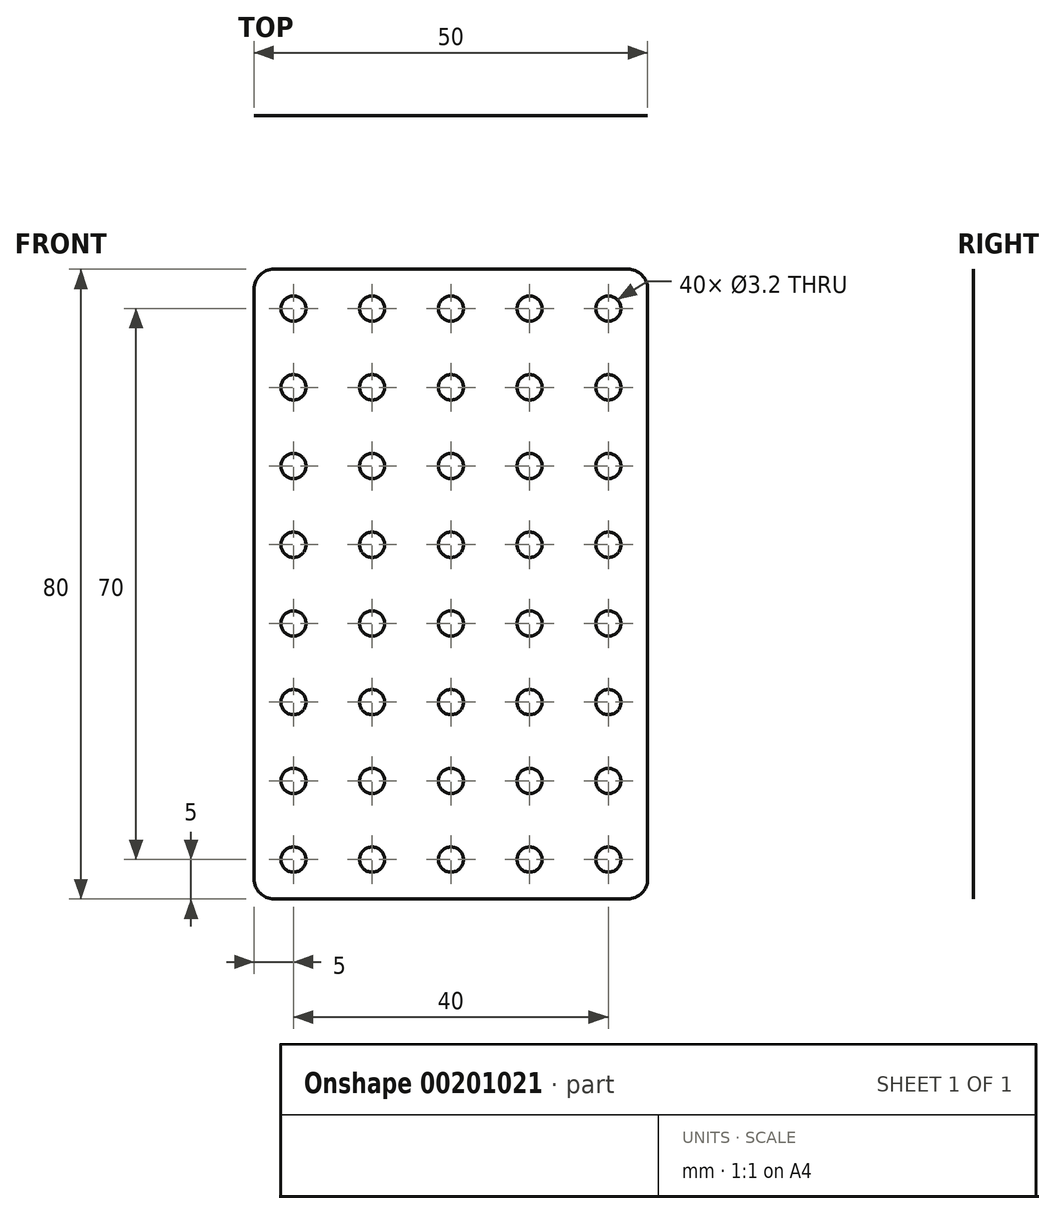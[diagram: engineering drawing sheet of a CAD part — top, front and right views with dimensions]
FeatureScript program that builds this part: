
annotation { "Feature Type Name" : "Feature", "Feature Type Description" : "" }
export const myFeature = defineFeature(function(context is Context, id is Id, definition is map)
    precondition{}
    {
        {
            var Q0;
            Q0=qCreatedBy(makeId("Front.planeOp"),FACE);
            var sketch = newSketch(context, id + "F0", { "sketchPlane" : qUnion([Q0])});
            skLineSegment(sketch, "E0.bottom", {"start": v(2.54, 0) * mm, "end": v(47.46, 0) * mm});
            skLineSegment(sketch, "E0.top", {"start": v(2.54, -80) * mm, "end": v(47.46, -80) * mm});
            skLineSegment(sketch, "E0.left", {"start": v(0, -2.54) * mm, "end": v(0, -77.46) * mm});
            skLineSegment(sketch, "E0.right", {"start": v(50, -2.54) * mm, "end": v(50, -77.46) * mm});
            skPoint(sketch, "E1.visualSharp", {"position": v(0, 0) * mm});
            skArc(sketch, "E1.filletArc", {"start": v(2.54, 0) * mm, "mid": v(0.74, -0.74) * mm, "end": v(0, -2.54) * mm});
            skPoint(sketch, "E2.visualSharp", {"position": v(50, 0) * mm});
            skArc(sketch, "E2.filletArc", {"start": v(50, -2.54) * mm, "mid": v(49.26, -0.74) * mm, "end": v(47.46, 0) * mm});
            skPoint(sketch, "E3.visualSharp", {"position": v(0, -80) * mm});
            skArc(sketch, "E3.filletArc", {"start": v(0, -77.46) * mm, "mid": v(0.74, -79.26) * mm, "end": v(2.54, -80) * mm});
            skPoint(sketch, "E4.visualSharp", {"position": v(50, -80) * mm});
            skArc(sketch, "E4.filletArc", {"start": v(47.46, -80) * mm, "mid": v(49.26, -79.26) * mm, "end": v(50, -77.46) * mm});
            skCircle(sketch, "E5", {"center": v(5, -5) * mm, "radius": 1.6 * mm});
            skCircle(sketch, "E6.0.1.0", {"center": v(5, -15) * mm, "radius": 1.6 * mm});
            skCircle(sketch, "E6.0.2.0", {"center": v(5, -25) * mm, "radius": 1.6 * mm});
            skCircle(sketch, "E6.0.3.0", {"center": v(5, -35) * mm, "radius": 1.6 * mm});
            skCircle(sketch, "E6.0.4.0", {"center": v(5, -45) * mm, "radius": 1.6 * mm});
            skCircle(sketch, "E6.0.5.0", {"center": v(5, -55) * mm, "radius": 1.6 * mm});
            skCircle(sketch, "E6.0.6.0", {"center": v(5, -65) * mm, "radius": 1.6 * mm});
            skCircle(sketch, "E6.0.7.0", {"center": v(5, -75) * mm, "radius": 1.6 * mm});
            skCircle(sketch, "E6.1.0.0", {"center": v(15, -5) * mm, "radius": 1.6 * mm});
            skCircle(sketch, "E6.1.1.0", {"center": v(15, -15) * mm, "radius": 1.6 * mm});
            skCircle(sketch, "E6.1.2.0", {"center": v(15, -25) * mm, "radius": 1.6 * mm});
            skCircle(sketch, "E6.1.3.0", {"center": v(15, -35) * mm, "radius": 1.6 * mm});
            skCircle(sketch, "E6.1.4.0", {"center": v(15, -45) * mm, "radius": 1.6 * mm});
            skCircle(sketch, "E6.1.5.0", {"center": v(15, -55) * mm, "radius": 1.6 * mm});
            skCircle(sketch, "E6.1.6.0", {"center": v(15, -65) * mm, "radius": 1.6 * mm});
            skCircle(sketch, "E6.1.7.0", {"center": v(15, -75) * mm, "radius": 1.6 * mm});
            skCircle(sketch, "E6.2.0.0", {"center": v(25, -5) * mm, "radius": 1.6 * mm});
            skCircle(sketch, "E6.2.1.0", {"center": v(25, -15) * mm, "radius": 1.6 * mm});
            skCircle(sketch, "E6.2.2.0", {"center": v(25, -25) * mm, "radius": 1.6 * mm});
            skCircle(sketch, "E6.2.3.0", {"center": v(25, -35) * mm, "radius": 1.6 * mm});
            skCircle(sketch, "E6.2.4.0", {"center": v(25, -45) * mm, "radius": 1.6 * mm});
            skCircle(sketch, "E6.2.5.0", {"center": v(25, -55) * mm, "radius": 1.6 * mm});
            skCircle(sketch, "E6.2.6.0", {"center": v(25, -65) * mm, "radius": 1.6 * mm});
            skCircle(sketch, "E6.2.7.0", {"center": v(25, -75) * mm, "radius": 1.6 * mm});
            skCircle(sketch, "E6.3.0.0", {"center": v(35, -5) * mm, "radius": 1.6 * mm});
            skCircle(sketch, "E6.3.1.0", {"center": v(35, -15) * mm, "radius": 1.6 * mm});
            skCircle(sketch, "E6.3.2.0", {"center": v(35, -25) * mm, "radius": 1.6 * mm});
            skCircle(sketch, "E6.3.3.0", {"center": v(35, -35) * mm, "radius": 1.6 * mm});
            skCircle(sketch, "E6.3.4.0", {"center": v(35, -45) * mm, "radius": 1.6 * mm});
            skCircle(sketch, "E6.3.5.0", {"center": v(35, -55) * mm, "radius": 1.6 * mm});
            skCircle(sketch, "E6.3.6.0", {"center": v(35, -65) * mm, "radius": 1.6 * mm});
            skCircle(sketch, "E6.3.7.0", {"center": v(35, -75) * mm, "radius": 1.6 * mm});
            skCircle(sketch, "E6.4.0.0", {"center": v(45, -5) * mm, "radius": 1.6 * mm});
            skCircle(sketch, "E6.4.1.0", {"center": v(45, -15) * mm, "radius": 1.6 * mm});
            skCircle(sketch, "E6.4.2.0", {"center": v(45, -25) * mm, "radius": 1.6 * mm});
            skCircle(sketch, "E6.4.3.0", {"center": v(45, -35) * mm, "radius": 1.6 * mm});
            skCircle(sketch, "E6.4.4.0", {"center": v(45, -45) * mm, "radius": 1.6 * mm});
            skCircle(sketch, "E6.4.5.0", {"center": v(45, -55) * mm, "radius": 1.6 * mm});
            skCircle(sketch, "E6.4.6.0", {"center": v(45, -65) * mm, "radius": 1.6 * mm});
            skCircle(sketch, "E6.4.7.0", {"center": v(45, -75) * mm, "radius": 1.6 * mm});
            skLineSegment(sketch, "E6.direction1", {"start": v(5, -5) * mm, "end": v(15, -5) * mm, "construction": true});
            skLineSegment(sketch, "E6.direction2", {"start": v(5, -5) * mm, "end": v(5, -15) * mm, "construction": true});
            skSolve(sketch);
        }
        {
            var Q0;
            Q0=makeQuery(id+"F0.imprint","IMPRINT",FACE,{"disambiguationData":[TD([[makeQuery(id+"F0.imprint","IMPRINT",EDGE,{"derivedFrom":sQuery(id+"F0.wireOp",EDGE,"E0.bottom")}),-1.0]])]});
            extrude(context, id + "F1", {"entities" : qUnion([Q0]), "depth" : 1 / 203.2 * mm});
        }
    });
